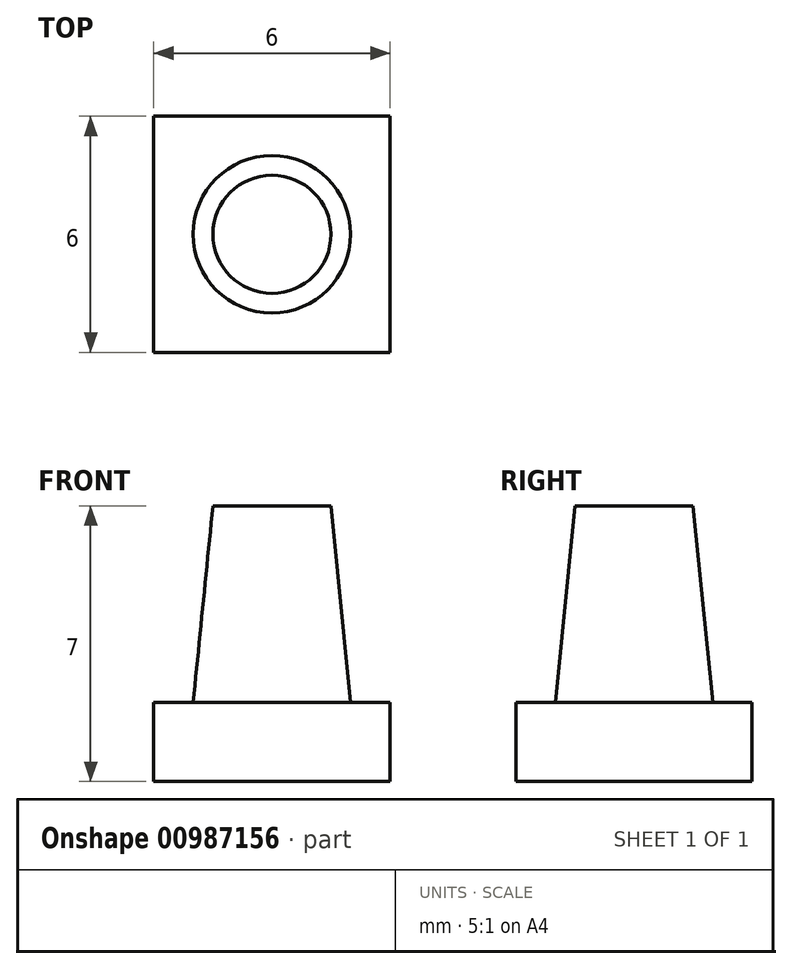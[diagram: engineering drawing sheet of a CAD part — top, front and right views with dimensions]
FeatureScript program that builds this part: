
annotation { "Feature Type Name" : "Feature", "Feature Type Description" : "" }
export const myFeature = defineFeature(function(context is Context, id is Id, definition is map)
    precondition{}
    {
        {
            var Q0;
            Q0=qCreatedBy(makeId("Front.planeOp"),FACE);
            var sketch = newSketch(context, id + "F0", { "sketchPlane" : qUnion([Q0])});
            skLineSegment(sketch, "E0", {"start": v(0, 0) * mm, "end": v(0, 15.93) * mm, "construction": true});
            skLineSegment(sketch, "E1", {"start": v(0, 0) * mm, "end": v(0, 5) * mm});
            skLineSegment(sketch, "E2", {"start": v(0, 5) * mm, "end": v(-1.5, 5) * mm});
            skLineSegment(sketch, "E3", {"start": v(-1.5, 5) * mm, "end": v(-2, 0) * mm});
            skLineSegment(sketch, "E4", {"start": v(-2, 0) * mm, "end": v(0, 0) * mm});
            skSolve(sketch);
        }
        {
            var Q0;
            Q0=makeQuery(id+"F0.imprint","IMPRINT",FACE,{"disambiguationData":[TD([[makeQuery(id+"F0.imprint","IMPRINT",EDGE,{"derivedFrom":sQuery(id+"F0.wireOp",EDGE,"E1")}),1.0]])]});
            var Q1;
            Q1=sQuery(id+"F0.wireOp",EDGE,"E0");
            revolve(context, id + "F1", {"surfaceOperationType" : NewSurfaceOperationType.NEW, "entities" : qUnion([Q0]), "axis" : qUnion([Q1]), "revolveType" : RevolveType.FULL});
        }
        {
            var Q0;
            Q0=makeQuery(id+"F1.opRevolve","SWEPT_FACE",FACE,{"disambiguationData":[OSD([sQuery(id+"F0.wireOp",EDGE,"E4")])]});
            var sketch = newSketch(context, id + "F2", { "sketchPlane" : qUnion([Q0])});
            skLineSegment(sketch, "E5.bottom", {"start": v(3, -3) * mm, "end": v(-3, -3) * mm});
            skLineSegment(sketch, "E5.top", {"start": v(3, 3) * mm, "end": v(-3, 3) * mm});
            skLineSegment(sketch, "E5.left", {"start": v(3, -3) * mm, "end": v(3, 3) * mm});
            skLineSegment(sketch, "E5.right", {"start": v(-3, -3) * mm, "end": v(-3, 3) * mm});
            skPoint(sketch, "E5.middle", {"position": v(0, 0) * mm});
            skSolve(sketch);
        }
        {
            var Q0;
            Q0=makeQuery(id+"F2.imprint","IMPRINT",FACE,{"disambiguationData":[TD([[makeQuery(id+"F2.imprint","IMPRINT",EDGE,{"derivedFrom":sQuery(id+"F2.wireOp",EDGE,"E5.bottom")}),-1.0]])]});
            var Q1;
            Q1=makeQuery(id+"F2.imprint","IMPRINT",FACE,{"disambiguationData":[TD([[makeQuery(id+"F2.imprint","IMPRINT",EDGE,{"derivedFrom":makeQuery(id+"F1.opRevolve","SWEPT_EDGE",EDGE,{"disambiguationData":[OSD([sQuery(id+"F0.wireOp",EDGE,"E3"),sQuery(id+"F0.wireOp",EDGE,"E4")])]})}),1.0]])]});
            extrude(context, id + "F3", {"entities" : qUnion([Q0, Q1]), "operationType" : NewBodyOperationType.ADD, "depth" : 2 * mm, "offsetDistance" : 25 * mm});
        }
    });
